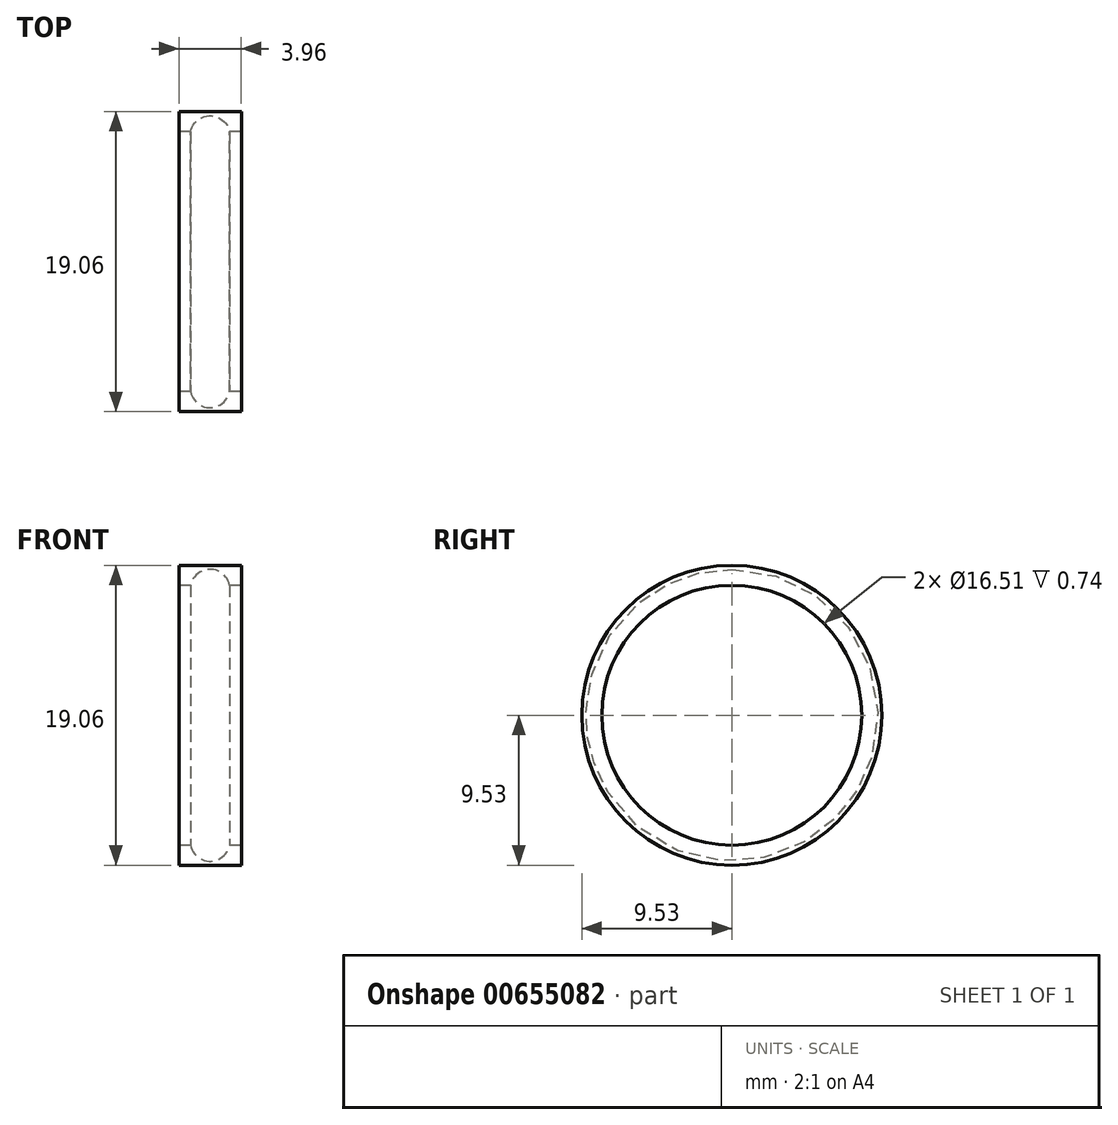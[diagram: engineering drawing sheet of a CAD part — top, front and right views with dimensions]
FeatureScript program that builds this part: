
annotation { "Feature Type Name" : "Feature", "Feature Type Description" : "" }
export const myFeature = defineFeature(function(context is Context, id is Id, definition is map)
    precondition{}
    {
        {
            var Q0;
            Q0=qCreatedBy(makeId("Front.planeOp"),FACE);
            var sketch = newSketch(context, id + "F0", { "sketchPlane" : qUnion([Q0])});
            skLineSegment(sketch, "E0.bottom", {"start": v(-1.98, 9.53) * mm, "end": v(1.98, 9.53) * mm});
            skLineSegment(sketch, "E0.left", {"start": v(-1.98, 9.53) * mm, "end": v(-1.98, 8.26) * mm});
            skLineSegment(sketch, "E0.right", {"start": v(1.98, 9.53) * mm, "end": v(1.98, 8.26) * mm});
            skLineSegment(sketch, "E1", {"start": v(-8.37, 0) * mm, "end": v(11.75, 0) * mm});
            skLineSegment(sketch, "E2", {"start": v(-1.98, 8.26) * mm, "end": v(-1.24, 8.26) * mm});
            skArc(sketch, "E3", {"start": v(1.24, 8.25) * mm, "mid": v(0, 9.27) * mm, "end": v(-1.24, 8.25) * mm});
            skLineSegment(sketch, "E4.trimOffspring", {"start": v(1.24, 8.26) * mm, "end": v(1.98, 8.26) * mm});
            skSolve(sketch);
        }
        {
            var Q0;
            Q0 = qSketchRegion(id + "F0", true);
            var Q1;
            Q1=sQuery(id+"F0.wireOp",EDGE,"E1");
            revolve(context, id + "F1", {"entities" : qUnion([Q0]), "axis" : qUnion([Q1]), "revolveType" : RevolveType.FULL});
        }
    });
